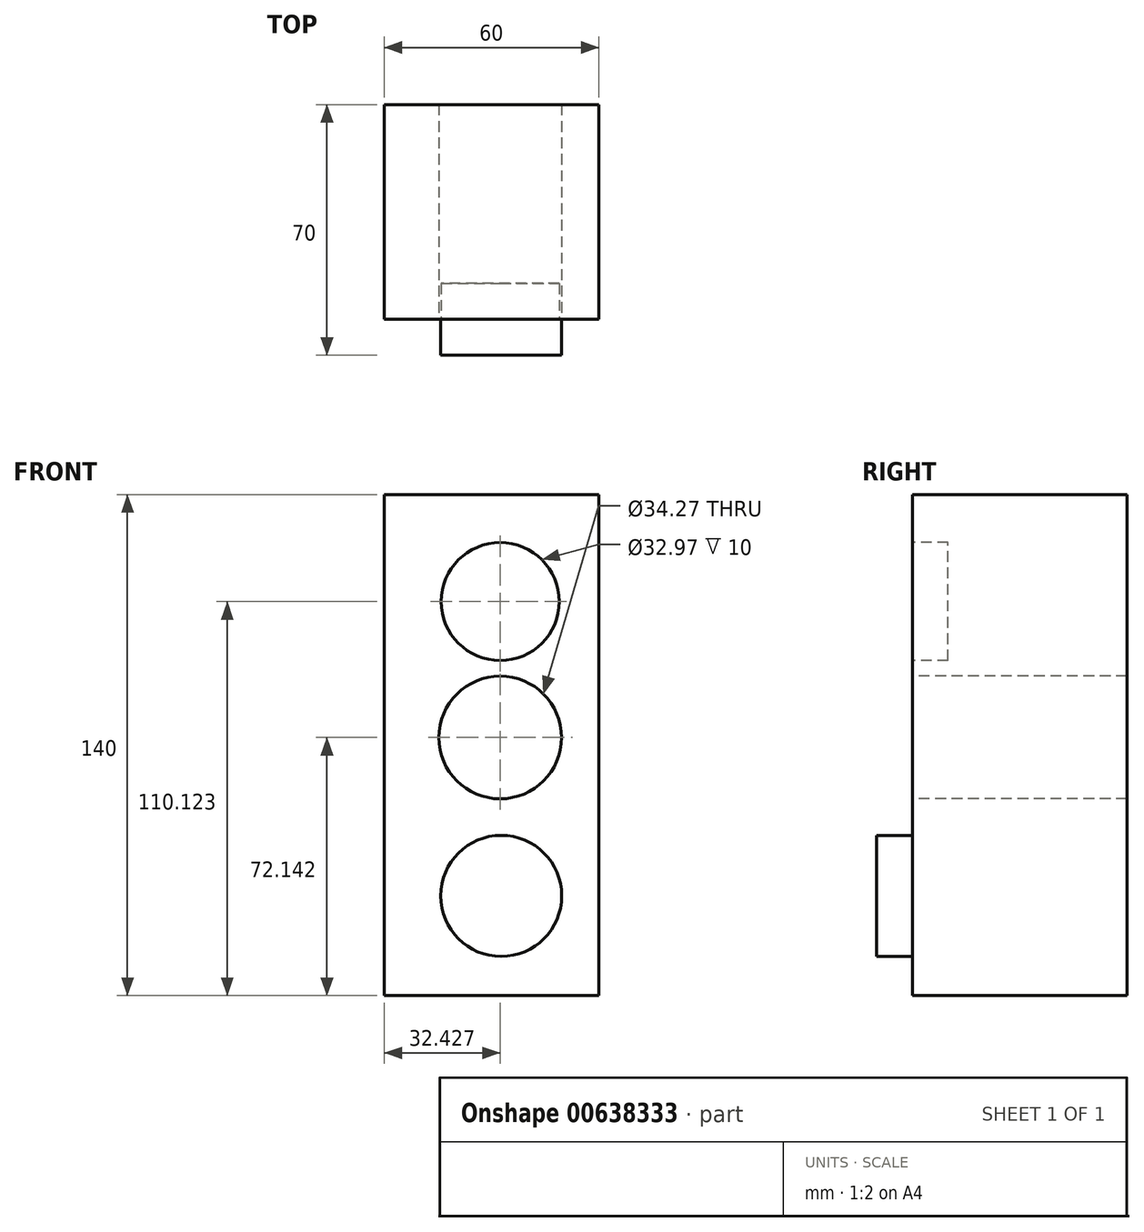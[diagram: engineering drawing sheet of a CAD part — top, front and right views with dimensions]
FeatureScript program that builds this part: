
annotation { "Feature Type Name" : "Feature", "Feature Type Description" : "" }
export const myFeature = defineFeature(function(context is Context, id is Id, definition is map)
    precondition{}
    {
        {
            var Q0;
            Q0=qCreatedBy(makeId("Top.planeOp"),FACE);
            var sketch = newSketch(context, id + "F0", { "sketchPlane" : qUnion([Q0])});
            skLineSegment(sketch, "E0.bottom", {"start": v(0, 0) * mm, "end": v(60, 0) * mm});
            skLineSegment(sketch, "E0.top", {"start": v(0, 60) * mm, "end": v(60, 60) * mm});
            skLineSegment(sketch, "E0.left", {"start": v(0, 0) * mm, "end": v(0, 60) * mm});
            skLineSegment(sketch, "E0.right", {"start": v(60, 0) * mm, "end": v(60, 60) * mm});
            skSolve(sketch);
        }
        {
            var Q0;
            Q0 = qSketchRegion(id + "F0", true);
            extrude(context, id + "F1", {"entities" : qUnion([Q0]), "depth" : 140 * mm, "offsetDistance" : 25 * mm});
        }
        {
            var Q0;
            Q0=makeQuery(id+"F1.opExtrude","SWEPT_FACE",FACE,{"disambiguationData":[OSD([sQuery(id+"F0.wireOp",EDGE,"E0.bottom")])]});
            var sketch = newSketch(context, id + "F2", { "sketchPlane" : qUnion([Q0])});
            skCircle(sketch, "E1", {"center": v(32.43, 110.12) * mm, "radius": 16.48 * mm});
            skCircle(sketch, "E2", {"center": v(32.43, 72.14) * mm, "radius": 17.14 * mm});
            skCircle(sketch, "E3", {"center": v(32.71, 27.88) * mm, "radius": 16.9 * mm});
            skSolve(sketch);
        }
        {
            var Q0;
            Q0 = qSketchRegion(id + "F2", true);
            extrude(context, id + "F3", {"entities" : qUnion([Q0]), "operationType" : NewBodyOperationType.ADD, "depth" : 15 * mm, "offsetDistance" : 25 * mm});
        }
        {
            var Q0;
            Q0=makeQuery(id+"F3.opExtrude","CAP_FACE",FACE,{"disambiguationData":[OSD([sQuery(id+"F2.wireOp",EDGE,"E2")])],"isStart":false});
            extrude(context, id + "F4", {"entities" : qUnion([Q0]), "operationType" : NewBodyOperationType.REMOVE, "oppositeDirection" : true, "depth" : 199 * mm, "offsetDistance" : 25 * mm});
        }
        {
            var Q0;
            Q0=makeQuery(id+"F3.opExtrude","CAP_FACE",FACE,{"disambiguationData":[OSD([sQuery(id+"F2.wireOp",EDGE,"E1")])],"isStart":false});
            extrude(context, id + "F5", {"entities" : qUnion([Q0]), "operationType" : NewBodyOperationType.REMOVE, "oppositeDirection" : true, "depth" : 25 * mm, "offsetDistance" : 25 * mm});
        }
        {
            var Q0;
            Q0=makeQuery(id+"F3.opExtrude","CAP_FACE",FACE,{"disambiguationData":[OSD([sQuery(id+"F2.wireOp",EDGE,"E3")])],"isStart":false});
            extrude(context, id + "F6", {"entities" : qUnion([Q0]), "operationType" : NewBodyOperationType.REMOVE, "oppositeDirection" : true, "depth" : 5 * mm, "offsetDistance" : 25 * mm});
        }
    });
